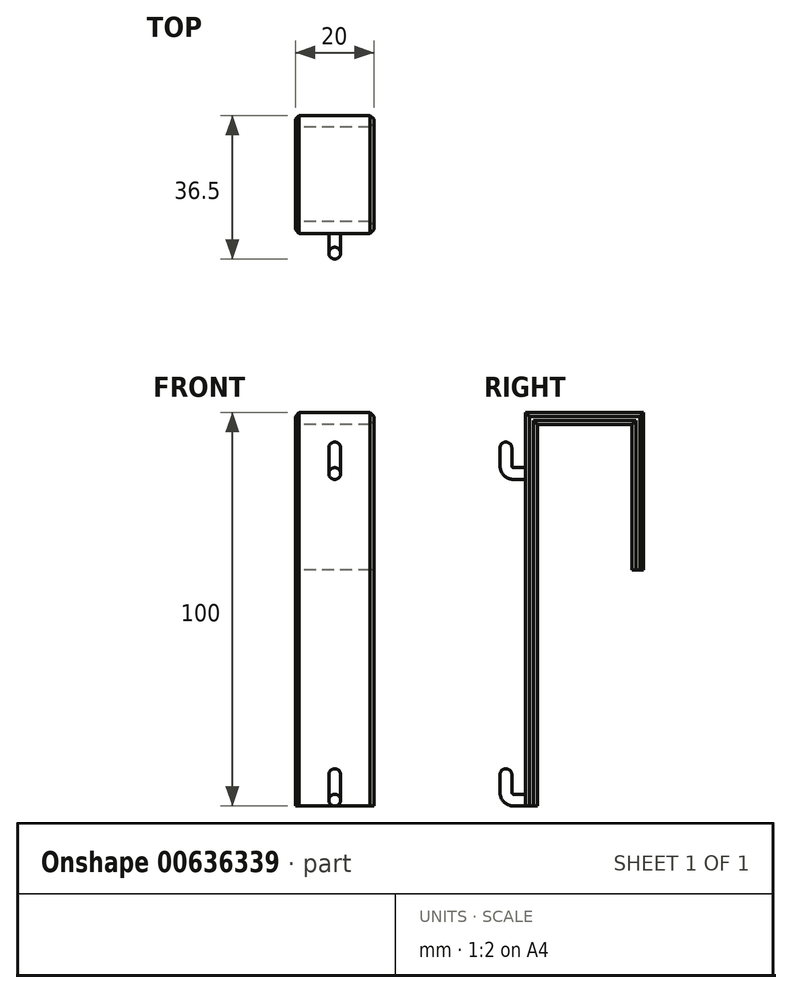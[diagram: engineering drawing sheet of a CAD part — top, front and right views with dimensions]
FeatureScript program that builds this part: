
annotation { "Feature Type Name" : "Feature", "Feature Type Description" : "" }
export const myFeature = defineFeature(function(context is Context, id is Id, definition is map)
    precondition{}
    {
        {
            var Q0;
            Q0=qCreatedBy(makeId("Right.planeOp"),FACE);
            var sketch = newSketch(context, id + "F0", { "sketchPlane" : qUnion([Q0])});
            skLineSegment(sketch, "E0.bottom", {"start": v(0, 0) * mm, "end": v(-30, 0) * mm});
            skLineSegment(sketch, "E0.left", {"start": v(0, 0) * mm, "end": v(0, -40) * mm});
            skLineSegment(sketch, "E0.right", {"start": v(-30, 0) * mm, "end": v(-30, -100) * mm});
            skLineSegment(sketch, "E1.bottom", {"start": v(-27, -3) * mm, "end": v(-3, -3) * mm});
            skLineSegment(sketch, "E1.left", {"start": v(-27, -3) * mm, "end": v(-27, -100) * mm});
            skLineSegment(sketch, "E1.right", {"start": v(-3, -3) * mm, "end": v(-3, -40) * mm});
            skLineSegment(sketch, "E2", {"start": v(-3, -40) * mm, "end": v(0, -40) * mm});
            skLineSegment(sketch, "E3.trimOffspring", {"start": v(-27, -100) * mm, "end": v(-30, -100) * mm});
            skSolve(sketch);
        }
        {
            var Q0;
            Q0 = qSketchRegion(id + "F0", true);
            extrude(context, id + "F1", {"entities" : qUnion([Q0]), "endBound" : BoundingType.SYMMETRIC, "depth" : 20 * mm, "offsetDistance" : 25 * mm});
        }
        {
            var Q0;
            Q0=qCreatedBy(makeId("Right.planeOp"),FACE);
            var sketch = newSketch(context, id + "F2", { "sketchPlane" : qUnion([Q0])});
            skLineSegment(sketch, "E4", {"start": v(-30, -98.5) * mm, "end": v(-33, -98.5) * mm});
            skLineSegment(sketch, "E5", {"start": v(-35, -96.5) * mm, "end": v(-35, -90.5) * mm});
            skPoint(sketch, "E6.visualSharp", {"position": v(-35, -98.5) * mm});
            skArc(sketch, "E6.filletArc", {"start": v(-35, -96.5) * mm, "mid": v(-34.41, -97.91) * mm, "end": v(-33, -98.5) * mm});
            skSolve(sketch);
        }
        {
            var Q0;
            Q0=makeQuery(id+"F1.opExtrude","SWEPT_FACE",FACE,{"disambiguationData":[OSD([sQuery(id+"F0.wireOp",EDGE,"E0.right")])]});
            var sketch = newSketch(context, id + "F3", { "sketchPlane" : qUnion([Q0])});
            skCircle(sketch, "E7", {"center": v(0, -98.5) * mm, "radius": 1.5 * mm});
            skSolve(sketch);
        }
        {
            var Q0;
            Q0 = qSketchRegion(id + "F3", true);
            var Q1;
            Q1 = qConstructionFilter(qBodyType(qCreatedBy(id + "F2" ,EDGE), BodyType.WIRE), ConstructionObject.NO);
            sweep(context, id + "F4", {"operationType" : NewBodyOperationType.ADD, "profiles" : qUnion([Q0]), "path" : qUnion([Q1])});
        }
        {
            var Q0;
            Q0=makeQuery(id+"F4.opSweep","CAP_EDGE",EDGE,{"disambiguationData":[OSD([sQuery(id+"F2.wireOp",VERTEX,"E5.end"),sQuery(id+"F3.wireOp",EDGE,"E7")])],"isStart":false});
            var Q1;
            Q1=makeQuery(id+"F4.opSweep","CAP_EDGE",EDGE,{"disambiguationData":[OSD([sQuery(id+"F2.wireOp",VERTEX,"E4.start"),sQuery(id+"F3.wireOp",EDGE,"E7")])],"isStart":true});
            fillet(context, id + "F5", {"entities" : qUnion([Q0, Q1]), "radius" : 1.5 * mm, "tangentPropagation" : true, "allowEdgeOverflow" : false});
        }
        {
            var Q0;
            Q0=qCreatedBy(makeId("Right.planeOp"),FACE);
            var sketch = newSketch(context, id + "F6", { "sketchPlane" : qUnion([Q0])});
            skLineSegment(sketch, "E8", {"start": v(-35, -7.5) * mm, "end": v(-35, -13.5) * mm});
            skLineSegment(sketch, "E9", {"start": v(-33, -15.5) * mm, "end": v(-30, -15.5) * mm});
            skPoint(sketch, "E10.visualSharp", {"position": v(-35, -15.5) * mm});
            skArc(sketch, "E10.filletArc", {"start": v(-35, -13.5) * mm, "mid": v(-34.41, -14.91) * mm, "end": v(-33, -15.5) * mm});
            skSolve(sketch);
        }
        {
            var Q0;
            Q0=makeQuery(id+"F1.opExtrude","SWEPT_FACE",FACE,{"disambiguationData":[OSD([sQuery(id+"F0.wireOp",EDGE,"E0.right")])]});
            var sketch = newSketch(context, id + "F7", { "sketchPlane" : qUnion([Q0])});
            skCircle(sketch, "E11", {"center": v(0, -15.5) * mm, "radius": 1.5 * mm});
            skSolve(sketch);
        }
        {
            var Q0;
            Q0 = qSketchRegion(id + "F7", true);
            var Q1;
            Q1 = qConstructionFilter(qBodyType(qCreatedBy(id + "F6" ,EDGE), BodyType.WIRE), ConstructionObject.NO);
            sweep(context, id + "F8", {"operationType" : NewBodyOperationType.ADD, "profiles" : qUnion([Q0]), "path" : qUnion([Q1])});
        }
        {
            var Q0;
            Q0=makeQuery(id+"F8.opSweep","CAP_EDGE",EDGE,{"disambiguationData":[OSD([sQuery(id+"F6.wireOp",VERTEX,"E8.start"),sQuery(id+"F7.wireOp",EDGE,"E11")])],"isStart":false});
            fillet(context, id + "F9", {"entities" : qUnion([Q0]), "radius" : 1.5 * mm, "tangentPropagation" : true, "allowEdgeOverflow" : false});
        }
        {
            var Q0;
            Q0=makeQuery(id+"F1.opExtrude","CAP_EDGE",EDGE,{"disambiguationData":[OSD([sQuery(id+"F0.wireOp",EDGE,"E0.right")])],"isStart":false});
            var Q1;
            Q1=makeQuery(id+"F1.opExtrude","CAP_EDGE",EDGE,{"disambiguationData":[OSD([sQuery(id+"F0.wireOp",EDGE,"E0.bottom")])],"isStart":false});
            var Q2;
            Q2=makeQuery(id+"F1.opExtrude","CAP_EDGE",EDGE,{"disambiguationData":[OSD([sQuery(id+"F0.wireOp",EDGE,"E0.left")])],"isStart":false});
            var Q3;
            Q3=makeQuery(id+"F1.opExtrude","CAP_EDGE",EDGE,{"disambiguationData":[OSD([sQuery(id+"F0.wireOp",EDGE,"E1.right")])],"isStart":false});
            var Q4;
            Q4=makeQuery(id+"F1.opExtrude","CAP_EDGE",EDGE,{"disambiguationData":[OSD([sQuery(id+"F0.wireOp",EDGE,"E1.bottom")])],"isStart":false});
            var Q5;
            Q5=makeQuery(id+"F1.opExtrude","CAP_EDGE",EDGE,{"disambiguationData":[OSD([sQuery(id+"F0.wireOp",EDGE,"E1.left")])],"isStart":false});
            var Q6;
            Q6=makeQuery(id+"F1.opExtrude","CAP_EDGE",EDGE,{"disambiguationData":[OSD([sQuery(id+"F0.wireOp",EDGE,"E0.right")])],"isStart":true});
            var Q7;
            Q7=makeQuery(id+"F1.opExtrude","CAP_EDGE",EDGE,{"disambiguationData":[OSD([sQuery(id+"F0.wireOp",EDGE,"E1.left")])],"isStart":true});
            var Q8;
            Q8=makeQuery(id+"F1.opExtrude","CAP_EDGE",EDGE,{"disambiguationData":[OSD([sQuery(id+"F0.wireOp",EDGE,"E0.bottom")])],"isStart":true});
            var Q9;
            Q9=makeQuery(id+"F1.opExtrude","CAP_EDGE",EDGE,{"disambiguationData":[OSD([sQuery(id+"F0.wireOp",EDGE,"E1.bottom")])],"isStart":true});
            var Q10;
            Q10=makeQuery(id+"F1.opExtrude","CAP_EDGE",EDGE,{"disambiguationData":[OSD([sQuery(id+"F0.wireOp",EDGE,"E1.right")])],"isStart":true});
            var Q11;
            Q11=makeQuery(id+"F1.opExtrude","CAP_EDGE",EDGE,{"disambiguationData":[OSD([sQuery(id+"F0.wireOp",EDGE,"E0.left")])],"isStart":true});
            chamfer(context, id + "F10", {"entities" : qUnion([Q0, Q1, Q2, Q3, Q4, Q5, Q6, Q7, Q8, Q9, Q10, Q11]), "width" : 1 * mm, "tangentPropagation" : true});
        }
    });
